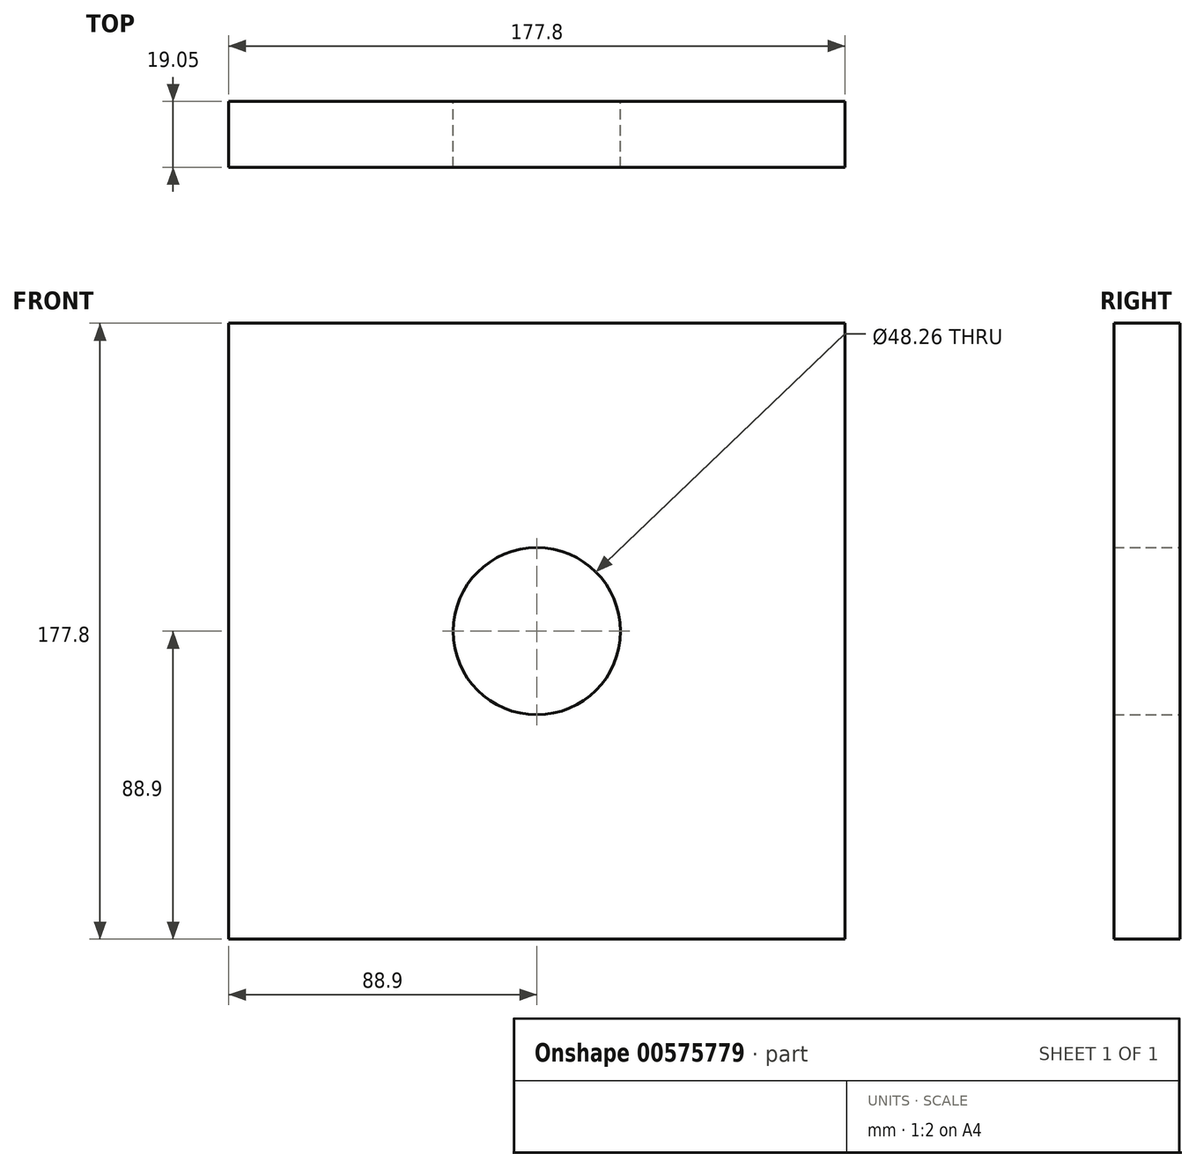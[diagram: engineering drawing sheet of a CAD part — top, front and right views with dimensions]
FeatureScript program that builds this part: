
annotation { "Feature Type Name" : "Feature", "Feature Type Description" : "" }
export const myFeature = defineFeature(function(context is Context, id is Id, definition is map)
    precondition{}
    {
        {
            var Q0;
            Q0=qCreatedBy(makeId("Front.planeOp"),FACE);
            var sketch = newSketch(context, id + "F0", { "sketchPlane" : qUnion([Q0])});
            skLineSegment(sketch, "E0.bottom", {"start": v(-88.9, -88.9) * mm, "end": v(88.9, -88.9) * mm});
            skLineSegment(sketch, "E0.top", {"start": v(-88.9, 88.9) * mm, "end": v(88.9, 88.9) * mm});
            skLineSegment(sketch, "E0.left", {"start": v(-88.9, -88.9) * mm, "end": v(-88.9, 88.9) * mm});
            skLineSegment(sketch, "E0.right", {"start": v(88.9, -88.9) * mm, "end": v(88.9, 88.9) * mm});
            skPoint(sketch, "E0.middle", {"position": v(0, 0) * mm});
            skCircle(sketch, "E1", {"center": v(0, 0) * mm, "radius": 24.13 * mm});
            skSolve(sketch);
        }
        {
            var Q0;
            Q0 = qSketchRegion(id + "F0", true);
            extrude(context, id + "F1", {"entities" : qUnion([Q0]), "depth" : 19.05 * mm, "offsetDistance" : 25.4 * mm});
        }
    });
